# Revit family: AISC MT Shapes-Side
name_source: partatom
category: Detail Items
revit_build: Autodesk Revit Architecture 2012 (Build: 20110210_1515)
units: mm (PartAtom-declared; Revit-internal decimal feet)

## types (14) — shared parameters
Keynote = 05 12 00.H0
y = 0' - 1 17/32"

## per-type parameters (varying)
| type | A | W | bf | d | k | tf | tw |
| MT6.25X6.2 | 0.01 SF | 6.2 | 0' - 3 3/4" | 0' - 6 9/32" | 0' - 0 9/16" | 0' - 0 7/32" | 0' - 0 5/32" |
| MT6.25X5.9 | 0.01 SF | 5.9 | 0' - 3 1/2" | 0' - 6 1/4" | 0' - 0 9/16" | 0' - 0 7/32" | 0' - 0 5/32" |
| MT6X5.9 | 0.01 SF | 5.9 | 0' - 3 1/16" | 0' - 6" | 0' - 0 9/16" | 0' - 0 7/32" | 0' - 0 3/16" |
| MT6X5.4 | 0.01 SF | 5.4 | 0' - 3 1/16" | 0' - 6" | 0' - 0 9/16" | 0' - 0 7/32" | 0' - 0 5/32" |
| MT6X5 | 0.01 SF | 5 | 0' - 3 1/4" | 0' - 6" | 0' - 0 1/2" | 0' - 0 3/16" | 0' - 0 5/32" |
| MT5X4.5 | 0.01 SF | 4.5 | 0' - 2 11/16" | 0' - 5" | 0' - 0 9/16" | 0' - 0 7/32" | 0' - 0 5/32" |
| MT5X4 | 0.01 SF | 4 | 0' - 2 11/16" | 0' - 4 31/32" | 0' - 0 9/16" | 0' - 0 3/16" | 0' - 0 5/32" |
| MT5X3.75 | 0.01 SF | 3.75 | 0' - 2 11/16" | 0' - 5" | 0' - 0 7/16" | 0' - 0 3/16" | 0' - 0 1/8" |
| MT4X3.25 | 0.01 SF | 3.25 | 0' - 2 9/32" | 0' - 4" | 0' - 0 9/16" | 0' - 0 3/16" | 0' - 0 1/8" |
| MT4X3.1 | 0.01 SF | 3.1 | 0' - 2 9/32" | 0' - 4" | 0' - 0 7/16" | 0' - 0 3/16" | 0' - 0 1/8" |
| MT3X2.2 | 0 SF | 2.2 | 0' - 1 27/32" | 0' - 3" | 0' - 0 3/8" | 0' - 0 5/32" | 0' - 0 1/8" |
| MT3X1.85 | 0 SF | 1.85 | 0' - 2" | 0' - 2 31/32" | 0' - 0 5/16" | 0' - 0 1/8" | 0' - 0 3/32" |
| MT2.5X9.45 | 0.02 SF | 9.45 | 0' - 5" | 0' - 2 1/2" | 0' - 0 13/16" | 0' - 0 13/32" | 0' - 0 5/16" |
| MT2X3 | 0.01 SF | 3 | 0' - 3 13/16" | 0' - 1 29/32" | 0' - 0 1/2" | 0' - 0 5/32" | 0' - 0 1/8" |

## geometry (parser evidence)
native form markers: Sweep x1
no freeform markers — native parametric forms only
